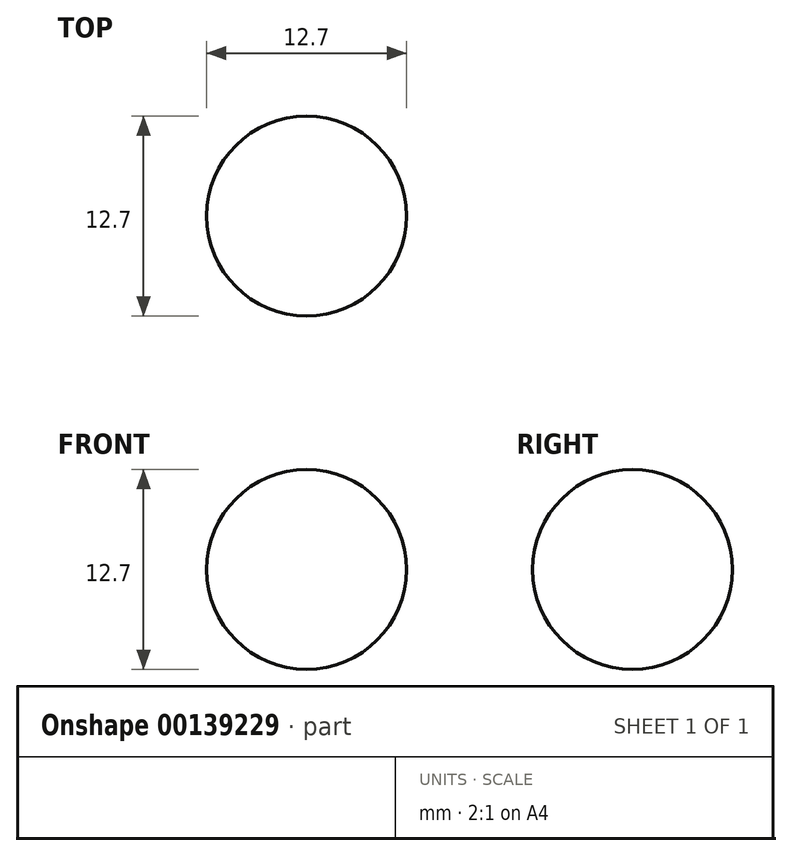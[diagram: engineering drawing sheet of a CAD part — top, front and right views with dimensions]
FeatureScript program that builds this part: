
annotation { "Feature Type Name" : "Feature", "Feature Type Description" : "" }
export const myFeature = defineFeature(function(context is Context, id is Id, definition is map)
    precondition{}
    {
        {
            var Q0;
            Q0=qCreatedBy(makeId("Front.planeOp"),FACE);
            var sketch = newSketch(context, id + "F0", { "sketchPlane" : qUnion([Q0])});
            skLineSegment(sketch, "E0", {"start": v(0, 0) * mm, "end": v(0, 12.7) * mm});
            skArc(sketch, "E1", {"start": v(0, 0) * mm, "mid": v(6.35, 6.35) * mm, "end": v(0, 12.7) * mm});
            skSolve(sketch);
        }
        {
            var Q0;
            Q0=makeQuery(id+"F0.imprint","IMPRINT",FACE,{"disambiguationData":[TD([[makeQuery(id+"F0.imprint","IMPRINT",EDGE,{"derivedFrom":sQuery(id+"F0.wireOp",EDGE,"E0")}),-1.0]])]});
            var Q1;
            Q1=sQuery(id+"F0.wireOp",EDGE,"E1");
            var Q2;
            Q2=sQuery(id+"F0.wireOp",EDGE,"E0");
            revolve(context, id + "F1", {"entities" : qUnion([Q0]), "surfaceEntities" : qUnion([Q1]), "axis" : qUnion([Q2]), "revolveType" : RevolveType.FULL});
        }
    });
